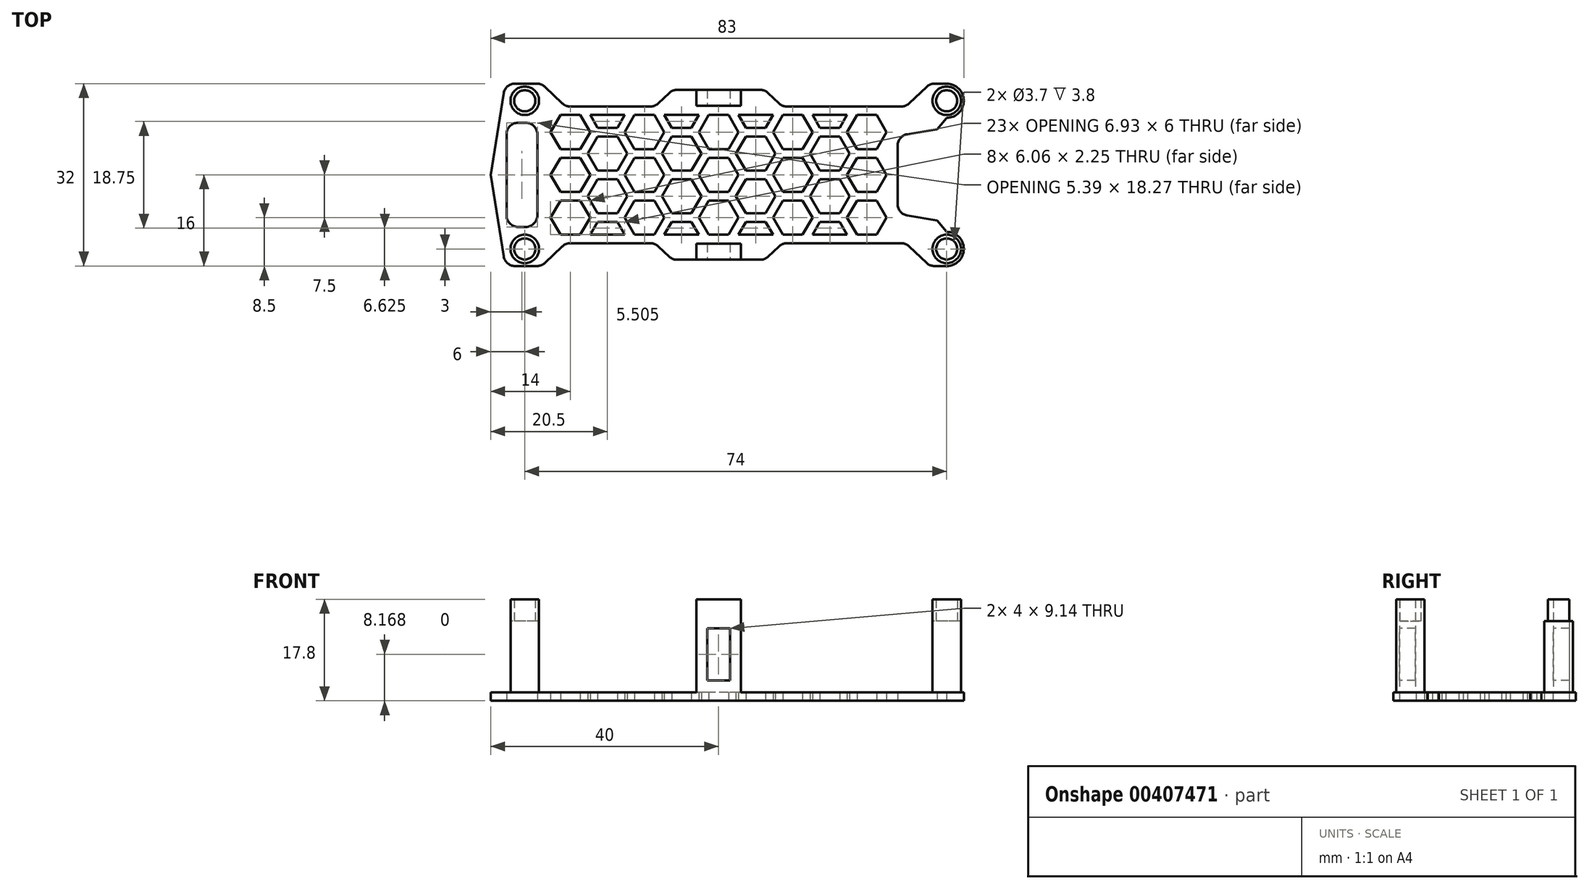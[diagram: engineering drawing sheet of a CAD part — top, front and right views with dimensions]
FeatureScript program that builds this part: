
annotation { "Feature Type Name" : "Feature", "Feature Type Description" : "" }
export const myFeature = defineFeature(function(context is Context, id is Id, definition is map)
    precondition{}
    {
        {
            var Q0;
            Q0=qCreatedBy(makeId("Top.planeOp"),FACE);
            var sketch = newSketch(context, id + "F0", { "sketchPlane" : qUnion([Q0])});
            skCircle(sketch, "E0", {"center": v(-34, 13) * mm, "radius": 1.85 * mm});
            skCircle(sketch, "E1", {"center": v(40, 13) * mm, "radius": 1.85 * mm});
            skCircle(sketch, "E2.MirrorC", {"center": v(-34, -13) * mm, "radius": 1.85 * mm});
            skCircle(sketch, "E3.MirrorC", {"center": v(40, -13) * mm, "radius": 1.85 * mm});
            skLineSegment(sketch, "E4", {"start": v(40, 10) * mm, "end": v(40, 8.3) * mm});
            skLineSegment(sketch, "E5", {"start": v(-37.43, 16) * mm, "end": v(-31.03, 16) * mm});
            skArc(sketch, "E6", {"start": v(40, 10) * mm, "mid": v(43, 13) * mm, "end": v(40, 16) * mm});
            skLineSegment(sketch, "E7.MirrorCS", {"start": v(40, -10) * mm, "end": v(40, -8.3) * mm});
            skArc(sketch, "E8.MirrorCS", {"start": v(40, -10) * mm, "mid": v(43, -13) * mm, "end": v(40, -16) * mm});
            skLineSegment(sketch, "E9.0", {"start": v(1.73, 4.5) * mm, "end": v(-1.73, 4.5) * mm});
            skLineSegment(sketch, "E9.1", {"start": v(-1.73, 4.5) * mm, "end": v(-3.46, 7.5) * mm});
            skLineSegment(sketch, "E9.2", {"start": v(-3.46, 7.5) * mm, "end": v(-1.73, 10.5) * mm});
            skLineSegment(sketch, "E9.3", {"start": v(-1.73, 10.5) * mm, "end": v(1.73, 10.5) * mm});
            skLineSegment(sketch, "E9.4", {"start": v(1.73, 10.5) * mm, "end": v(3.46, 7.5) * mm});
            skLineSegment(sketch, "E9.5", {"start": v(3.46, 7.5) * mm, "end": v(1.73, 4.5) * mm});
            skLineSegment(sketch, "E10.0", {"start": v(-1.73, 3) * mm, "end": v(1.73, 3) * mm});
            skLineSegment(sketch, "E10.1", {"start": v(1.73, 3) * mm, "end": v(3.46, 0) * mm});
            skLineSegment(sketch, "E10.2", {"start": v(3.46, 0) * mm, "end": v(1.73, -3) * mm});
            skLineSegment(sketch, "E10.3", {"start": v(1.73, -3) * mm, "end": v(-1.73, -3) * mm});
            skLineSegment(sketch, "E10.4", {"start": v(-1.73, -3) * mm, "end": v(-3.46, 0) * mm});
            skLineSegment(sketch, "E10.5", {"start": v(-3.46, 0) * mm, "end": v(-1.73, 3) * mm});
            skLineSegment(sketch, "E11.MirrorCS", {"start": v(-1.73, -4.5) * mm, "end": v(-3.46, -7.5) * mm});
            skLineSegment(sketch, "E12.MirrorCS", {"start": v(-3.46, -7.5) * mm, "end": v(-1.73, -10.5) * mm});
            skLineSegment(sketch, "E13.MirrorCS", {"start": v(-1.73, -10.5) * mm, "end": v(1.73, -10.5) * mm});
            skLineSegment(sketch, "E14.MirrorCS", {"start": v(1.73, -10.5) * mm, "end": v(3.46, -7.5) * mm});
            skLineSegment(sketch, "E15.MirrorCS", {"start": v(3.46, -7.5) * mm, "end": v(1.73, -4.5) * mm});
            skLineSegment(sketch, "E16.MirrorCS", {"start": v(1.73, -4.5) * mm, "end": v(-1.73, -4.5) * mm});
            skLineSegment(sketch, "E17.0", {"start": v(8.23, 0.75) * mm, "end": v(4.77, 0.75) * mm});
            skLineSegment(sketch, "E17.1", {"start": v(4.77, 0.75) * mm, "end": v(3.04, 3.75) * mm});
            skLineSegment(sketch, "E17.2", {"start": v(3.04, 3.75) * mm, "end": v(4.77, 6.75) * mm});
            skLineSegment(sketch, "E17.3", {"start": v(4.77, 6.75) * mm, "end": v(8.23, 6.75) * mm});
            skLineSegment(sketch, "E17.4", {"start": v(8.23, 6.75) * mm, "end": v(9.96, 3.75) * mm});
            skLineSegment(sketch, "E17.5", {"start": v(9.96, 3.75) * mm, "end": v(8.23, 0.75) * mm});
            skLineSegment(sketch, "E18.MirrorCS", {"start": v(9.96, -3.75) * mm, "end": v(8.23, -0.75) * mm});
            skLineSegment(sketch, "E19.MirrorCS", {"start": v(8.23, -6.75) * mm, "end": v(9.96, -3.75) * mm});
            skLineSegment(sketch, "E20.MirrorCS", {"start": v(4.77, -6.75) * mm, "end": v(8.23, -6.75) * mm});
            skLineSegment(sketch, "E21.MirrorCS", {"start": v(3.04, -3.75) * mm, "end": v(4.77, -6.75) * mm});
            skLineSegment(sketch, "E22.MirrorCS", {"start": v(4.77, -0.75) * mm, "end": v(3.04, -3.75) * mm});
            skLineSegment(sketch, "E23.MirrorCS", {"start": v(8.23, -0.75) * mm, "end": v(4.77, -0.75) * mm});
            skLineSegment(sketch, "E24.1.0.0", {"start": v(14.73, -3) * mm, "end": v(11.27, -3) * mm});
            skLineSegment(sketch, "E24.1.0.1", {"start": v(9.54, -7.5) * mm, "end": v(11.27, -10.5) * mm});
            skLineSegment(sketch, "E24.1.0.2", {"start": v(11.27, -3) * mm, "end": v(9.54, 0) * mm});
            skLineSegment(sketch, "E24.1.0.3", {"start": v(9.54, 7.5) * mm, "end": v(11.27, 10.5) * mm});
            skLineSegment(sketch, "E24.1.0.4", {"start": v(11.27, -10.5) * mm, "end": v(14.73, -10.5) * mm});
            skLineSegment(sketch, "E24.1.0.6", {"start": v(14.73, -4.5) * mm, "end": v(11.27, -4.5) * mm});
            skLineSegment(sketch, "E24.1.0.7", {"start": v(9.54, 0) * mm, "end": v(11.27, 3) * mm});
            skLineSegment(sketch, "E24.1.0.8", {"start": v(11.27, 4.5) * mm, "end": v(9.54, 7.5) * mm});
            skLineSegment(sketch, "E24.1.0.10", {"start": v(11.27, 10.5) * mm, "end": v(14.73, 10.5) * mm});
            skLineSegment(sketch, "E24.1.0.11", {"start": v(11.27, -4.5) * mm, "end": v(9.54, -7.5) * mm});
            skLineSegment(sketch, "E24.1.0.12", {"start": v(11.27, 3) * mm, "end": v(14.73, 3) * mm});
            skLineSegment(sketch, "E24.1.0.13", {"start": v(14.73, 4.5) * mm, "end": v(11.27, 4.5) * mm});
            skLineSegment(sketch, "E24.1.0.14", {"start": v(14.73, 10.5) * mm, "end": v(16.46, 7.5) * mm});
            skLineSegment(sketch, "E24.1.0.15", {"start": v(16.46, 7.5) * mm, "end": v(14.73, 4.5) * mm});
            skLineSegment(sketch, "E24.1.0.16", {"start": v(14.73, 3) * mm, "end": v(16.46, 0) * mm});
            skLineSegment(sketch, "E24.1.0.17", {"start": v(16.46, 0) * mm, "end": v(14.73, -3) * mm});
            skLineSegment(sketch, "E24.1.0.18", {"start": v(16.46, -7.5) * mm, "end": v(14.73, -4.5) * mm});
            skLineSegment(sketch, "E24.1.0.19", {"start": v(14.73, -10.5) * mm, "end": v(16.46, -7.5) * mm});
            skLineSegment(sketch, "E24.2.0.0", {"start": v(27.73, -3) * mm, "end": v(24.27, -3) * mm});
            skLineSegment(sketch, "E24.2.0.1", {"start": v(22.54, -7.5) * mm, "end": v(24.27, -10.5) * mm});
            skLineSegment(sketch, "E24.2.0.2", {"start": v(24.27, -3) * mm, "end": v(22.54, 0) * mm});
            skLineSegment(sketch, "E24.2.0.3", {"start": v(22.54, 7.5) * mm, "end": v(24.27, 10.5) * mm});
            skLineSegment(sketch, "E24.2.0.4", {"start": v(24.27, -10.5) * mm, "end": v(27.73, -10.5) * mm});
            skLineSegment(sketch, "E24.2.0.6", {"start": v(27.73, -4.5) * mm, "end": v(24.27, -4.5) * mm});
            skLineSegment(sketch, "E24.2.0.7", {"start": v(22.54, 0) * mm, "end": v(24.27, 3) * mm});
            skLineSegment(sketch, "E24.2.0.8", {"start": v(24.27, 4.5) * mm, "end": v(22.54, 7.5) * mm});
            skLineSegment(sketch, "E24.2.0.10", {"start": v(24.27, 10.5) * mm, "end": v(27.73, 10.5) * mm});
            skLineSegment(sketch, "E24.2.0.11", {"start": v(24.27, -4.5) * mm, "end": v(22.54, -7.5) * mm});
            skLineSegment(sketch, "E24.2.0.12", {"start": v(24.27, 3) * mm, "end": v(27.73, 3) * mm});
            skLineSegment(sketch, "E24.2.0.13", {"start": v(27.73, 4.5) * mm, "end": v(24.27, 4.5) * mm});
            skLineSegment(sketch, "E24.2.0.14", {"start": v(27.73, 10.5) * mm, "end": v(29.46, 7.5) * mm});
            skLineSegment(sketch, "E24.2.0.15", {"start": v(29.46, 7.5) * mm, "end": v(27.73, 4.5) * mm});
            skLineSegment(sketch, "E24.2.0.16", {"start": v(27.73, 3) * mm, "end": v(29.46, 0) * mm});
            skLineSegment(sketch, "E24.2.0.17", {"start": v(29.46, 0) * mm, "end": v(27.73, -3) * mm});
            skLineSegment(sketch, "E24.2.0.18", {"start": v(29.46, -7.5) * mm, "end": v(27.73, -4.5) * mm});
            skLineSegment(sketch, "E24.2.0.19", {"start": v(27.73, -10.5) * mm, "end": v(29.46, -7.5) * mm});
            skLineSegment(sketch, "E25.1.0.0", {"start": v(-14.73, -10.5) * mm, "end": v(-11.27, -10.5) * mm});
            skLineSegment(sketch, "E25.1.0.1", {"start": v(-16.46, -7.5) * mm, "end": v(-14.73, -10.5) * mm});
            skLineSegment(sketch, "E25.1.0.4", {"start": v(-14.73, -4.5) * mm, "end": v(-16.46, -7.5) * mm});
            skLineSegment(sketch, "E25.1.0.5", {"start": v(-14.73, 10.5) * mm, "end": v(-11.27, 10.5) * mm});
            skLineSegment(sketch, "E25.1.0.6", {"start": v(-16.46, 0) * mm, "end": v(-14.73, 3) * mm});
            skLineSegment(sketch, "E25.1.0.7", {"start": v(-16.46, 7.5) * mm, "end": v(-14.73, 10.5) * mm});
            skLineSegment(sketch, "E25.1.0.8", {"start": v(-11.27, -3) * mm, "end": v(-14.73, -3) * mm});
            skLineSegment(sketch, "E25.1.0.9", {"start": v(-11.27, -4.5) * mm, "end": v(-14.73, -4.5) * mm});
            skLineSegment(sketch, "E25.1.0.10", {"start": v(-14.73, -3) * mm, "end": v(-16.46, 0) * mm});
            skLineSegment(sketch, "E25.1.0.11", {"start": v(-14.73, 4.5) * mm, "end": v(-16.46, 7.5) * mm});
            skLineSegment(sketch, "E25.1.0.12", {"start": v(-14.73, 3) * mm, "end": v(-11.27, 3) * mm});
            skLineSegment(sketch, "E25.1.0.13", {"start": v(-11.27, 4.5) * mm, "end": v(-14.73, 4.5) * mm});
            skLineSegment(sketch, "E25.1.0.14", {"start": v(-11.27, -10.5) * mm, "end": v(-9.54, -7.5) * mm});
            skLineSegment(sketch, "E25.1.0.15", {"start": v(-9.54, -7.5) * mm, "end": v(-11.27, -4.5) * mm});
            skLineSegment(sketch, "E25.1.0.16", {"start": v(-9.54, 0) * mm, "end": v(-11.27, -3) * mm});
            skLineSegment(sketch, "E25.1.0.17", {"start": v(-11.27, 3) * mm, "end": v(-9.54, 0) * mm});
            skLineSegment(sketch, "E25.1.0.18", {"start": v(-9.54, 7.5) * mm, "end": v(-11.27, 4.5) * mm});
            skLineSegment(sketch, "E25.1.0.19", {"start": v(-11.27, 10.5) * mm, "end": v(-9.54, 7.5) * mm});
            skLineSegment(sketch, "E25.2.0.0", {"start": v(-27.73, -10.5) * mm, "end": v(-24.27, -10.5) * mm});
            skLineSegment(sketch, "E25.2.0.1", {"start": v(-29.46, -7.5) * mm, "end": v(-27.73, -10.5) * mm});
            skLineSegment(sketch, "E25.2.0.4", {"start": v(-27.73, -4.5) * mm, "end": v(-29.46, -7.5) * mm});
            skLineSegment(sketch, "E25.2.0.5", {"start": v(-27.73, 10.5) * mm, "end": v(-24.27, 10.5) * mm});
            skLineSegment(sketch, "E25.2.0.6", {"start": v(-29.46, 0) * mm, "end": v(-27.73, 3) * mm});
            skLineSegment(sketch, "E25.2.0.7", {"start": v(-29.46, 7.5) * mm, "end": v(-27.73, 10.5) * mm});
            skLineSegment(sketch, "E25.2.0.8", {"start": v(-24.27, -3) * mm, "end": v(-27.73, -3) * mm});
            skLineSegment(sketch, "E25.2.0.9", {"start": v(-24.27, -4.5) * mm, "end": v(-27.73, -4.5) * mm});
            skLineSegment(sketch, "E25.2.0.10", {"start": v(-27.73, -3) * mm, "end": v(-29.46, 0) * mm});
            skLineSegment(sketch, "E25.2.0.11", {"start": v(-27.73, 4.5) * mm, "end": v(-29.46, 7.5) * mm});
            skLineSegment(sketch, "E25.2.0.12", {"start": v(-27.73, 3) * mm, "end": v(-24.27, 3) * mm});
            skLineSegment(sketch, "E25.2.0.13", {"start": v(-24.27, 4.5) * mm, "end": v(-27.73, 4.5) * mm});
            skLineSegment(sketch, "E25.2.0.14", {"start": v(-24.27, -10.5) * mm, "end": v(-22.54, -7.5) * mm});
            skLineSegment(sketch, "E25.2.0.15", {"start": v(-22.54, -7.5) * mm, "end": v(-24.27, -4.5) * mm});
            skLineSegment(sketch, "E25.2.0.16", {"start": v(-22.54, 0) * mm, "end": v(-24.27, -3) * mm});
            skLineSegment(sketch, "E25.2.0.17", {"start": v(-24.27, 3) * mm, "end": v(-22.54, 0) * mm});
            skLineSegment(sketch, "E25.2.0.18", {"start": v(-22.54, 7.5) * mm, "end": v(-24.27, 4.5) * mm});
            skLineSegment(sketch, "E25.2.0.19", {"start": v(-24.27, 10.5) * mm, "end": v(-22.54, 7.5) * mm});
            skLineSegment(sketch, "E26.1.0.0", {"start": v(16.04, 3.75) * mm, "end": v(17.77, 6.75) * mm});
            skLineSegment(sketch, "E26.1.0.1", {"start": v(17.77, 6.75) * mm, "end": v(21.23, 6.75) * mm});
            skLineSegment(sketch, "E26.1.0.2", {"start": v(21.23, 6.75) * mm, "end": v(22.96, 3.75) * mm});
            skLineSegment(sketch, "E26.1.0.3", {"start": v(22.96, 3.75) * mm, "end": v(21.23, 0.75) * mm});
            skLineSegment(sketch, "E26.1.0.4", {"start": v(21.23, 0.75) * mm, "end": v(17.77, 0.75) * mm});
            skLineSegment(sketch, "E26.1.0.5", {"start": v(17.77, 0.75) * mm, "end": v(16.04, 3.75) * mm});
            skLineSegment(sketch, "E26.1.0.6", {"start": v(17.77, -0.75) * mm, "end": v(16.04, -3.75) * mm});
            skLineSegment(sketch, "E26.1.0.7", {"start": v(21.23, -0.75) * mm, "end": v(17.77, -0.75) * mm});
            skLineSegment(sketch, "E26.1.0.8", {"start": v(22.96, -3.75) * mm, "end": v(21.23, -0.75) * mm});
            skLineSegment(sketch, "E26.1.0.9", {"start": v(21.23, -6.75) * mm, "end": v(22.96, -3.75) * mm});
            skLineSegment(sketch, "E26.1.0.10", {"start": v(17.77, -6.75) * mm, "end": v(21.23, -6.75) * mm});
            skLineSegment(sketch, "E26.1.0.11", {"start": v(16.04, -3.75) * mm, "end": v(17.77, -6.75) * mm});
            skLineSegment(sketch, "E27.1.0.0", {"start": v(-8.23, -0.75) * mm, "end": v(-9.96, -3.75) * mm});
            skLineSegment(sketch, "E27.1.0.1", {"start": v(-4.77, -6.75) * mm, "end": v(-3.04, -3.75) * mm});
            skLineSegment(sketch, "E27.1.0.3", {"start": v(-9.96, -3.75) * mm, "end": v(-8.23, -6.75) * mm});
            skLineSegment(sketch, "E27.1.0.4", {"start": v(-3.04, -3.75) * mm, "end": v(-4.77, -0.75) * mm});
            skLineSegment(sketch, "E27.1.0.5", {"start": v(-4.77, -0.75) * mm, "end": v(-8.23, -0.75) * mm});
            skLineSegment(sketch, "E27.1.0.6", {"start": v(-3.04, 3.75) * mm, "end": v(-4.77, 0.75) * mm});
            skLineSegment(sketch, "E27.1.0.7", {"start": v(-4.77, 6.75) * mm, "end": v(-3.04, 3.75) * mm});
            skLineSegment(sketch, "E27.1.0.8", {"start": v(-8.23, 6.75) * mm, "end": v(-4.77, 6.75) * mm});
            skLineSegment(sketch, "E27.1.0.9", {"start": v(-9.96, 3.75) * mm, "end": v(-8.23, 6.75) * mm});
            skLineSegment(sketch, "E27.1.0.10", {"start": v(-8.23, 0.75) * mm, "end": v(-9.96, 3.75) * mm});
            skLineSegment(sketch, "E27.1.0.11", {"start": v(-4.77, 0.75) * mm, "end": v(-8.23, 0.75) * mm});
            skLineSegment(sketch, "E27.2.0.0", {"start": v(-21.23, -0.75) * mm, "end": v(-22.96, -3.75) * mm});
            skLineSegment(sketch, "E27.2.0.1", {"start": v(-17.77, -6.75) * mm, "end": v(-16.04, -3.75) * mm});
            skLineSegment(sketch, "E27.2.0.3", {"start": v(-22.96, -3.75) * mm, "end": v(-21.23, -6.75) * mm});
            skLineSegment(sketch, "E27.2.0.4", {"start": v(-16.04, -3.75) * mm, "end": v(-17.77, -0.75) * mm});
            skLineSegment(sketch, "E27.2.0.5", {"start": v(-17.77, -0.75) * mm, "end": v(-21.23, -0.75) * mm});
            skLineSegment(sketch, "E27.2.0.6", {"start": v(-16.04, 3.75) * mm, "end": v(-17.77, 0.75) * mm});
            skLineSegment(sketch, "E27.2.0.7", {"start": v(-17.77, 6.75) * mm, "end": v(-16.04, 3.75) * mm});
            skLineSegment(sketch, "E27.2.0.8", {"start": v(-21.23, 6.75) * mm, "end": v(-17.77, 6.75) * mm});
            skLineSegment(sketch, "E27.2.0.9", {"start": v(-22.96, 3.75) * mm, "end": v(-21.23, 6.75) * mm});
            skLineSegment(sketch, "E27.2.0.10", {"start": v(-21.23, 0.75) * mm, "end": v(-22.96, 3.75) * mm});
            skLineSegment(sketch, "E27.2.0.11", {"start": v(-17.77, 0.75) * mm, "end": v(-21.23, 0.75) * mm});
            skLineSegment(sketch, "E28", {"start": v(-21.23, -6.75) * mm, "end": v(-17.77, -6.75) * mm});
            skLineSegment(sketch, "E29", {"start": v(-8.23, -6.75) * mm, "end": v(-4.77, -6.75) * mm});
            skLineSegment(sketch, "E30.MirrorCS", {"start": v(-22.53, 10.5) * mm, "end": v(-21.23, 8.25) * mm});
            skLineSegment(sketch, "E31.MirrorCS", {"start": v(-17.77, 8.25) * mm, "end": v(-16.47, 10.5) * mm});
            skLineSegment(sketch, "E32.MirrorCS", {"start": v(-21.23, 8.25) * mm, "end": v(-17.77, 8.25) * mm});
            skLineSegment(sketch, "E33", {"start": v(-22.53, 10.5) * mm, "end": v(-16.47, 10.5) * mm});
            skLineSegment(sketch, "E34.MirrorCS", {"start": v(-22.53, -10.5) * mm, "end": v(-21.23, -8.25) * mm});
            skLineSegment(sketch, "E35.MirrorCS", {"start": v(-21.23, -8.25) * mm, "end": v(-17.77, -8.25) * mm});
            skLineSegment(sketch, "E36.MirrorCS", {"start": v(-17.77, -8.25) * mm, "end": v(-16.47, -10.5) * mm});
            skLineSegment(sketch, "E37.MirrorCS", {"start": v(-22.53, -10.5) * mm, "end": v(-16.47, -10.5) * mm});
            skLineSegment(sketch, "E38.1.0.0", {"start": v(-9.53, 10.5) * mm, "end": v(-3.47, 10.5) * mm});
            skLineSegment(sketch, "E38.1.0.1", {"start": v(-9.53, 10.5) * mm, "end": v(-8.23, 8.25) * mm});
            skLineSegment(sketch, "E38.1.0.2", {"start": v(-8.23, 8.25) * mm, "end": v(-4.77, 8.25) * mm});
            skLineSegment(sketch, "E38.1.0.3", {"start": v(-4.77, 8.25) * mm, "end": v(-3.47, 10.5) * mm});
            skLineSegment(sketch, "E38.1.0.4", {"start": v(-4.77, -8.25) * mm, "end": v(-3.47, -10.5) * mm});
            skLineSegment(sketch, "E38.1.0.5", {"start": v(-8.23, -8.25) * mm, "end": v(-4.77, -8.25) * mm});
            skLineSegment(sketch, "E38.1.0.6", {"start": v(-9.53, -10.5) * mm, "end": v(-8.23, -8.25) * mm});
            skLineSegment(sketch, "E38.1.0.7", {"start": v(-9.53, -10.5) * mm, "end": v(-3.47, -10.5) * mm});
            skLineSegment(sketch, "E38.2.0.0", {"start": v(3.47, 10.5) * mm, "end": v(9.53, 10.5) * mm});
            skLineSegment(sketch, "E38.2.0.1", {"start": v(3.47, 10.5) * mm, "end": v(4.77, 8.25) * mm});
            skLineSegment(sketch, "E38.2.0.2", {"start": v(4.77, 8.25) * mm, "end": v(8.23, 8.25) * mm});
            skLineSegment(sketch, "E38.2.0.3", {"start": v(8.23, 8.25) * mm, "end": v(9.53, 10.5) * mm});
            skLineSegment(sketch, "E38.2.0.4", {"start": v(8.23, -8.25) * mm, "end": v(9.53, -10.5) * mm});
            skLineSegment(sketch, "E38.2.0.5", {"start": v(4.77, -8.25) * mm, "end": v(8.23, -8.25) * mm});
            skLineSegment(sketch, "E38.2.0.6", {"start": v(3.47, -10.5) * mm, "end": v(4.77, -8.25) * mm});
            skLineSegment(sketch, "E38.2.0.7", {"start": v(3.47, -10.5) * mm, "end": v(9.53, -10.5) * mm});
            skLineSegment(sketch, "E38.3.0.0", {"start": v(16.47, 10.5) * mm, "end": v(22.53, 10.5) * mm});
            skLineSegment(sketch, "E38.3.0.1", {"start": v(16.47, 10.5) * mm, "end": v(17.77, 8.25) * mm});
            skLineSegment(sketch, "E38.3.0.2", {"start": v(17.77, 8.25) * mm, "end": v(21.23, 8.25) * mm});
            skLineSegment(sketch, "E38.3.0.3", {"start": v(21.23, 8.25) * mm, "end": v(22.53, 10.5) * mm});
            skLineSegment(sketch, "E38.3.0.4", {"start": v(21.23, -8.25) * mm, "end": v(22.53, -10.5) * mm});
            skLineSegment(sketch, "E38.3.0.5", {"start": v(17.77, -8.25) * mm, "end": v(21.23, -8.25) * mm});
            skLineSegment(sketch, "E38.3.0.6", {"start": v(16.47, -10.5) * mm, "end": v(17.77, -8.25) * mm});
            skLineSegment(sketch, "E38.3.0.7", {"start": v(16.47, -10.5) * mm, "end": v(22.53, -10.5) * mm});
            skLineSegment(sketch, "E39", {"start": v(-31.03, 16) * mm, "end": v(-26.86, 12) * mm});
            skLineSegment(sketch, "E40.MirrorCS", {"start": v(-8.12, 14.9) * mm, "end": v(-11.14, 12) * mm});
            skLineSegment(sketch, "E41.MirrorCS", {"start": v(8.12, 14.9) * mm, "end": v(11.14, 12) * mm});
            skLineSegment(sketch, "E42.MirrorCS", {"start": v(37.03, 16) * mm, "end": v(32.86, 12) * mm});
            skLineSegment(sketch, "E43.trimOffspring", {"start": v(37.03, 16) * mm, "end": v(40, 16) * mm});
            skLineSegment(sketch, "E44.trimOffspring", {"start": v(-11.14, 12) * mm, "end": v(-26.86, 12) * mm});
            skLineSegment(sketch, "E45.trimOffspring", {"start": v(32.86, 12) * mm, "end": v(11.14, 12) * mm});
            skLineSegment(sketch, "E46.MirrorCS", {"start": v(-37.43, -16) * mm, "end": v(-31.03, -16) * mm});
            skLineSegment(sketch, "E47.MirrorCS", {"start": v(-31.03, -16) * mm, "end": v(-26.86, -12) * mm});
            skLineSegment(sketch, "E48.MirrorCS", {"start": v(-11.14, -12) * mm, "end": v(-26.86, -12) * mm});
            skLineSegment(sketch, "E49.MirrorCS", {"start": v(-8.12, -14.9) * mm, "end": v(-11.14, -12) * mm});
            skLineSegment(sketch, "E50.MirrorCS", {"start": v(8.12, -14.9) * mm, "end": v(11.14, -12) * mm});
            skLineSegment(sketch, "E51.MirrorCS", {"start": v(32.86, -12) * mm, "end": v(11.14, -12) * mm});
            skLineSegment(sketch, "E52.MirrorCS", {"start": v(37.03, -16) * mm, "end": v(32.86, -12) * mm});
            skLineSegment(sketch, "E53.MirrorCS", {"start": v(37.03, -16) * mm, "end": v(40, -16) * mm});
            skLineSegment(sketch, "E54", {"start": v(40, 8.3) * mm, "end": v(31.39, 6.82) * mm});
            skLineSegment(sketch, "E55", {"start": v(31.39, 6.82) * mm, "end": v(31.39, 0) * mm});
            skLineSegment(sketch, "E56.MirrorCS", {"start": v(31.39, -6.82) * mm, "end": v(31.39, 0) * mm});
            skLineSegment(sketch, "E57.MirrorCS", {"start": v(40, -8.3) * mm, "end": v(31.39, -6.82) * mm});
            skLineSegment(sketch, "E58.bottom", {"start": v(-31.8, 9.13) * mm, "end": v(-37.19, 9.13) * mm});
            skLineSegment(sketch, "E58.top", {"start": v(-31.8, -9.13) * mm, "end": v(-37.19, -9.13) * mm});
            skLineSegment(sketch, "E58.left", {"start": v(-31.8, 9.13) * mm, "end": v(-31.8, -9.13) * mm});
            skLineSegment(sketch, "E58.right", {"start": v(-37.19, 9.13) * mm, "end": v(-37.19, -9.13) * mm});
            skPoint(sketch, "E58.middle", {"position": v(-34.5, 0) * mm});
            skCircle(sketch, "E59", {"center": v(-34, 13) * mm, "radius": 2.5 * mm});
            skCircle(sketch, "E60", {"center": v(40, 13) * mm, "radius": 2.5 * mm});
            skCircle(sketch, "E61.MirrorC", {"center": v(-34, -13) * mm, "radius": 2.5 * mm});
            skCircle(sketch, "E62.MirrorC", {"center": v(40, -13) * mm, "radius": 2.5 * mm});
            skLineSegment(sketch, "E63.bottom", {"start": v(3.9, 12.1) * mm, "end": v(-3.9, 12.1) * mm});
            skLineSegment(sketch, "E63.top", {"start": v(3.9, 14.9) * mm, "end": v(-3.9, 14.9) * mm});
            skLineSegment(sketch, "E63.left", {"start": v(3.9, 12.1) * mm, "end": v(3.9, 14.9) * mm});
            skLineSegment(sketch, "E63.right", {"start": v(-3.9, 12.1) * mm, "end": v(-3.9, 14.9) * mm});
            skPoint(sketch, "E63.middle", {"position": v(0, 13.5) * mm});
            skLineSegment(sketch, "E64.MirrorCS", {"start": v(-3.9, -12.1) * mm, "end": v(-3.9, -14.9) * mm});
            skLineSegment(sketch, "E65.MirrorCS", {"start": v(3.9, -14.9) * mm, "end": v(-3.9, -14.9) * mm});
            skLineSegment(sketch, "E66.MirrorCS", {"start": v(3.9, -12.1) * mm, "end": v(3.9, -14.9) * mm});
            skLineSegment(sketch, "E67.MirrorCS", {"start": v(3.9, -12.1) * mm, "end": v(-3.9, -12.1) * mm});
            skLineSegment(sketch, "E68", {"start": v(-8.12, 14.9) * mm, "end": v(8.12, 14.9) * mm});
            skLineSegment(sketch, "E69", {"start": v(-8.12, -14.9) * mm, "end": v(8.12, -14.9) * mm});
            skLineSegment(sketch, "E70", {"start": v(-40, 0) * mm, "end": v(-37.43, 16) * mm});
            skLineSegment(sketch, "E71.MirrorCS", {"start": v(-40, 0) * mm, "end": v(-37.43, -16) * mm});
            skSolve(sketch);
        }
        {
            var Q0;
            Q0=makeQuery(id+"F0.imprint","IMPRINT",FACE,{"disambiguationData":[TD([[makeQuery(id+"F0.imprint","IMPRINT",EDGE,{"derivedFrom":sQuery(id+"F0.wireOp",EDGE,"E4")}),-1.0]])]});
            extrude(context, id + "F1", {"entities" : qUnion([Q0]), "depth" : 1.5 * mm});
        }
        {
            var Q0;
            Q0=makeQuery(id+"F0.imprint","IMPRINT",FACE,{"disambiguationData":[TD([[makeQuery(id+"F0.imprint","IMPRINT",EDGE,{"derivedFrom":sQuery(id+"F0.wireOp",EDGE,"E3.MirrorC")}),1.0]])]});
            var Q1;
            Q1=makeQuery(id+"F0.imprint","IMPRINT",FACE,{"disambiguationData":[TD([[makeQuery(id+"F0.imprint","IMPRINT",EDGE,{"derivedFrom":sQuery(id+"F0.wireOp",EDGE,"E1")}),-1.0]])]});
            var Q2;
            Q2=makeQuery(id+"F0.imprint","IMPRINT",FACE,{"disambiguationData":[TD([[makeQuery(id+"F0.imprint","IMPRINT",EDGE,{"derivedFrom":sQuery(id+"F0.wireOp",EDGE,"E2.MirrorC")}),1.0]])]});
            var Q3;
            Q3=makeQuery(id+"F0.imprint","IMPRINT",FACE,{"disambiguationData":[TD([[makeQuery(id+"F0.imprint","IMPRINT",EDGE,{"derivedFrom":sQuery(id+"F0.wireOp",EDGE,"E0")}),-1.0]])]});
            extrude(context, id + "F2", {"entities" : qUnion([Q0, Q1, Q2, Q3]), "operationType" : NewBodyOperationType.ADD, "depth" : 14 * mm});
        }
        {
            var Q0;
            Q0=makeQuery(id+"F0.imprint","IMPRINT",FACE,{"disambiguationData":[TD([[makeQuery(id+"F0.imprint","IMPRINT",EDGE,{"derivedFrom":sQuery(id+"F0.wireOp",EDGE,"E2.MirrorC")}),-1.0]])]});
            var Q1;
            Q1=makeQuery(id+"F0.imprint","IMPRINT",FACE,{"disambiguationData":[TD([[makeQuery(id+"F0.imprint","IMPRINT",EDGE,{"derivedFrom":sQuery(id+"F0.wireOp",EDGE,"E0")}),1.0]])]});
            var Q2;
            Q2=makeQuery(id+"F0.imprint","IMPRINT",FACE,{"disambiguationData":[TD([[makeQuery(id+"F0.imprint","IMPRINT",EDGE,{"derivedFrom":sQuery(id+"F0.wireOp",EDGE,"E1")}),1.0]])]});
            var Q3;
            Q3=makeQuery(id+"F0.imprint","IMPRINT",FACE,{"disambiguationData":[TD([[makeQuery(id+"F0.imprint","IMPRINT",EDGE,{"derivedFrom":sQuery(id+"F0.wireOp",EDGE,"E3.MirrorC")}),-1.0]])]});
            var Q4;
            Q4=makeQuery(id+"F0.imprint","IMPRINT",FACE,{"disambiguationData":[TD([[makeQuery(id+"F0.imprint","IMPRINT",EDGE,{"derivedFrom":sQuery(id+"F0.wireOp",EDGE,"E63.bottom")}),-1.0]])]});
            var Q5;
            {var subQ0=sQuery(id+"F0.wireOp",EDGE,"E64.MirrorCS");Q5=makeQuery(id+"F0.imprint","IMPRINT",FACE,{"disambiguationData":[TD([[makeQuery(id+"F0.imprint","IMPRINT",EDGE,{"derivedFrom":subQ0}),1.0]])]});}
            extrude(context, id + "F3", {"entities" : qUnion([Q0, Q1, Q2, Q3, Q4, Q5]), "operationType" : NewBodyOperationType.ADD, "depth" : 17.8 * mm});
        }
        {
            var Q0;
            {var subQ0=sQuery(id+"F0.wireOp",EDGE,"E69");Q0=makeQuery(id+"F3.boolean.opBoolean","MERGE",FACE,{"derivedFrom":[makeQuery(id+"F1.opExtrude","SWEPT_FACE",FACE,{"disambiguationData":[OSD([subQ0]),TDD([makeQuery(id+"F0.imprint","IMPRINT",EDGE,{"disambiguationData":[TD([[makeQuery(id+"F0.imprint","INTERSECT",VERTEX,{"derivedFrom":[sQuery(id+"F0.wireOp",EDGE,"E49.MirrorCS"),subQ0]}),-1.0]])],"derivedFrom":subQ0})])]}),makeQuery(id+"F1.opExtrude","SWEPT_FACE",FACE,{"disambiguationData":[OSD([subQ0]),TDD([makeQuery(id+"F0.imprint","IMPRINT",EDGE,{"disambiguationData":[TD([[makeQuery(id+"F0.imprint","INTERSECT",VERTEX,{"derivedFrom":[sQuery(id+"F0.wireOp",EDGE,"E50.MirrorCS"),subQ0]}),1.0]])],"derivedFrom":subQ0})])]}),makeQuery(id+"F3.opExtrude","SWEPT_FACE",FACE,{"disambiguationData":[OSD([subQ0])]})]});}
            var sketch = newSketch(context, id + "F4", { "sketchPlane" : qUnion([Q0])});
            skLineSegment(sketch, "E72.bottom", {"start": v(2, 3.6) * mm, "end": v(-2, 3.6) * mm});
            skLineSegment(sketch, "E72.top", {"start": v(2, 12.74) * mm, "end": v(-2, 12.74) * mm});
            skLineSegment(sketch, "E72.left", {"start": v(2, 3.6) * mm, "end": v(2, 12.74) * mm});
            skLineSegment(sketch, "E72.right", {"start": v(-2, 3.6) * mm, "end": v(-2, 12.74) * mm});
            skPoint(sketch, "E72.middle", {"position": v(0, 8.17) * mm});
            skSolve(sketch);
        }
        {
            var Q0;
            Q0=makeQuery(id+"F4.imprint","IMPRINT",FACE,{"disambiguationData":[TD([[makeQuery(id+"F4.imprint","IMPRINT",EDGE,{"derivedFrom":sQuery(id+"F4.wireOp",EDGE,"E72.bottom")}),-1.0]])]});
            extrude(context, id + "F5", {"entities" : qUnion([Q0]), "operationType" : NewBodyOperationType.REMOVE, "oppositeDirection" : true, "depth" : 32 * mm});
        }
        {
            var Q0;
            Q0=makeQuery(id+"F1.opExtrude","SWEPT_EDGE",EDGE,{"disambiguationData":[OSD([sQuery(id+"F0.wireOp",EDGE,"E4"),sQuery(id+"F0.wireOp",EDGE,"E54")])]});
            var Q1;
            Q1=makeQuery(id+"F1.opExtrude","SWEPT_EDGE",EDGE,{"disambiguationData":[OSD([sQuery(id+"F0.wireOp",EDGE,"E7.MirrorCS"),sQuery(id+"F0.wireOp",EDGE,"E57.MirrorCS")])]});
            chamfer(context, id + "F6", {"entities" : qUnion([Q0, Q1]), "width" : 2 * mm, "tangentPropagation" : true});
        }
        {
            var Q0;
            Q0=makeQuery(id+"F1.opExtrude","SWEPT_EDGE",EDGE,{"disambiguationData":[OSD([sQuery(id+"F0.wireOp",EDGE,"E56.MirrorCS"),sQuery(id+"F0.wireOp",EDGE,"E57.MirrorCS")])]});
            var Q1;
            Q1=makeQuery(id+"F1.opExtrude","SWEPT_EDGE",EDGE,{"disambiguationData":[OSD([sQuery(id+"F0.wireOp",EDGE,"E54"),sQuery(id+"F0.wireOp",EDGE,"E55")])]});
            var Q2;
            Q2=makeQuery(id+"F1.opExtrude","SWEPT_EDGE",EDGE,{"disambiguationData":[OSD([sQuery(id+"F0.wireOp",EDGE,"E58.bottom"),sQuery(id+"F0.wireOp",EDGE,"E58.left")])]});
            var Q3;
            Q3=makeQuery(id+"F1.opExtrude","SWEPT_EDGE",EDGE,{"disambiguationData":[OSD([sQuery(id+"F0.wireOp",EDGE,"E58.bottom"),sQuery(id+"F0.wireOp",EDGE,"E58.right")])]});
            var Q4;
            Q4=makeQuery(id+"F1.opExtrude","SWEPT_EDGE",EDGE,{"disambiguationData":[OSD([sQuery(id+"F0.wireOp",EDGE,"E58.top"),sQuery(id+"F0.wireOp",EDGE,"E58.right")])]});
            var Q5;
            Q5=makeQuery(id+"F1.opExtrude","SWEPT_EDGE",EDGE,{"disambiguationData":[OSD([sQuery(id+"F0.wireOp",EDGE,"E58.top"),sQuery(id+"F0.wireOp",EDGE,"E58.left")])]});
            var Q6;
            Q6=makeQuery(id+"F1.opExtrude","SWEPT_EDGE",EDGE,{"disambiguationData":[OSD([sQuery(id+"F0.wireOp",EDGE,"E5"),sQuery(id+"F0.wireOp",EDGE,"E70")])]});
            var Q7;
            Q7=makeQuery(id+"F1.opExtrude","SWEPT_EDGE",EDGE,{"disambiguationData":[OSD([sQuery(id+"F0.wireOp",EDGE,"E46.MirrorCS"),sQuery(id+"F0.wireOp",EDGE,"E71.MirrorCS")])]});
            var Q8;
            Q8=makeQuery(id+"F1.opExtrude","SWEPT_EDGE",EDGE,{"disambiguationData":[OSD([sQuery(id+"F0.wireOp",EDGE,"E5"),sQuery(id+"F0.wireOp",EDGE,"E39")])]});
            var Q9;
            Q9=makeQuery(id+"F1.opExtrude","SWEPT_EDGE",EDGE,{"disambiguationData":[OSD([sQuery(id+"F0.wireOp",EDGE,"E39"),sQuery(id+"F0.wireOp",EDGE,"E44.trimOffspring")])]});
            var Q10;
            Q10=makeQuery(id+"F1.opExtrude","SWEPT_EDGE",EDGE,{"disambiguationData":[OSD([sQuery(id+"F0.wireOp",EDGE,"E40.MirrorCS"),sQuery(id+"F0.wireOp",EDGE,"E44.trimOffspring")])]});
            var Q11;
            Q11=makeQuery(id+"F1.opExtrude","SWEPT_EDGE",EDGE,{"disambiguationData":[OSD([sQuery(id+"F0.wireOp",EDGE,"E40.MirrorCS"),sQuery(id+"F0.wireOp",EDGE,"E68")])]});
            var Q12;
            Q12=makeQuery(id+"F1.opExtrude","SWEPT_EDGE",EDGE,{"disambiguationData":[OSD([sQuery(id+"F0.wireOp",EDGE,"E41.MirrorCS"),sQuery(id+"F0.wireOp",EDGE,"E68")])]});
            var Q13;
            Q13=makeQuery(id+"F1.opExtrude","SWEPT_EDGE",EDGE,{"disambiguationData":[OSD([sQuery(id+"F0.wireOp",EDGE,"E41.MirrorCS"),sQuery(id+"F0.wireOp",EDGE,"E45.trimOffspring")])]});
            var Q14;
            Q14=makeQuery(id+"F1.opExtrude","SWEPT_EDGE",EDGE,{"disambiguationData":[OSD([sQuery(id+"F0.wireOp",EDGE,"E42.MirrorCS"),sQuery(id+"F0.wireOp",EDGE,"E45.trimOffspring")])]});
            var Q15;
            Q15=makeQuery(id+"F1.opExtrude","SWEPT_EDGE",EDGE,{"disambiguationData":[OSD([sQuery(id+"F0.wireOp",EDGE,"E42.MirrorCS"),sQuery(id+"F0.wireOp",EDGE,"E43.trimOffspring")])]});
            var Q16;
            Q16=makeQuery(id+"F1.opExtrude","SWEPT_EDGE",EDGE,{"disambiguationData":[OSD([sQuery(id+"F0.wireOp",EDGE,"E52.MirrorCS"),sQuery(id+"F0.wireOp",EDGE,"E53.MirrorCS")])]});
            var Q17;
            Q17=makeQuery(id+"F1.opExtrude","SWEPT_EDGE",EDGE,{"disambiguationData":[OSD([sQuery(id+"F0.wireOp",EDGE,"E51.MirrorCS"),sQuery(id+"F0.wireOp",EDGE,"E52.MirrorCS")])]});
            var Q18;
            Q18=makeQuery(id+"F1.opExtrude","SWEPT_EDGE",EDGE,{"disambiguationData":[OSD([sQuery(id+"F0.wireOp",EDGE,"E50.MirrorCS"),sQuery(id+"F0.wireOp",EDGE,"E51.MirrorCS")])]});
            var Q19;
            Q19=makeQuery(id+"F1.opExtrude","SWEPT_EDGE",EDGE,{"disambiguationData":[OSD([sQuery(id+"F0.wireOp",EDGE,"E50.MirrorCS"),sQuery(id+"F0.wireOp",EDGE,"E69")])]});
            var Q20;
            Q20=makeQuery(id+"F1.opExtrude","SWEPT_EDGE",EDGE,{"disambiguationData":[OSD([sQuery(id+"F0.wireOp",EDGE,"E49.MirrorCS"),sQuery(id+"F0.wireOp",EDGE,"E69")])]});
            var Q21;
            Q21=makeQuery(id+"F1.opExtrude","SWEPT_EDGE",EDGE,{"disambiguationData":[OSD([sQuery(id+"F0.wireOp",EDGE,"E48.MirrorCS"),sQuery(id+"F0.wireOp",EDGE,"E49.MirrorCS")])]});
            var Q22;
            Q22=makeQuery(id+"F1.opExtrude","SWEPT_EDGE",EDGE,{"disambiguationData":[OSD([sQuery(id+"F0.wireOp",EDGE,"E47.MirrorCS"),sQuery(id+"F0.wireOp",EDGE,"E48.MirrorCS")])]});
            var Q23;
            Q23=makeQuery(id+"F1.opExtrude","SWEPT_EDGE",EDGE,{"disambiguationData":[OSD([sQuery(id+"F0.wireOp",EDGE,"E46.MirrorCS"),sQuery(id+"F0.wireOp",EDGE,"E47.MirrorCS")])]});
            fillet(context, id + "F7", {"entities" : qUnion([Q0, Q1, Q2, Q3, Q4, Q5, Q6, Q7, Q8, Q9, Q10, Q11, Q12, Q13, Q14, Q15, Q16, Q17, Q18, Q19, Q20, Q21, Q22, Q23]), "radius" : 2 * mm, "tangentPropagation" : true, "allowEdgeOverflow" : false});
        }
    });
